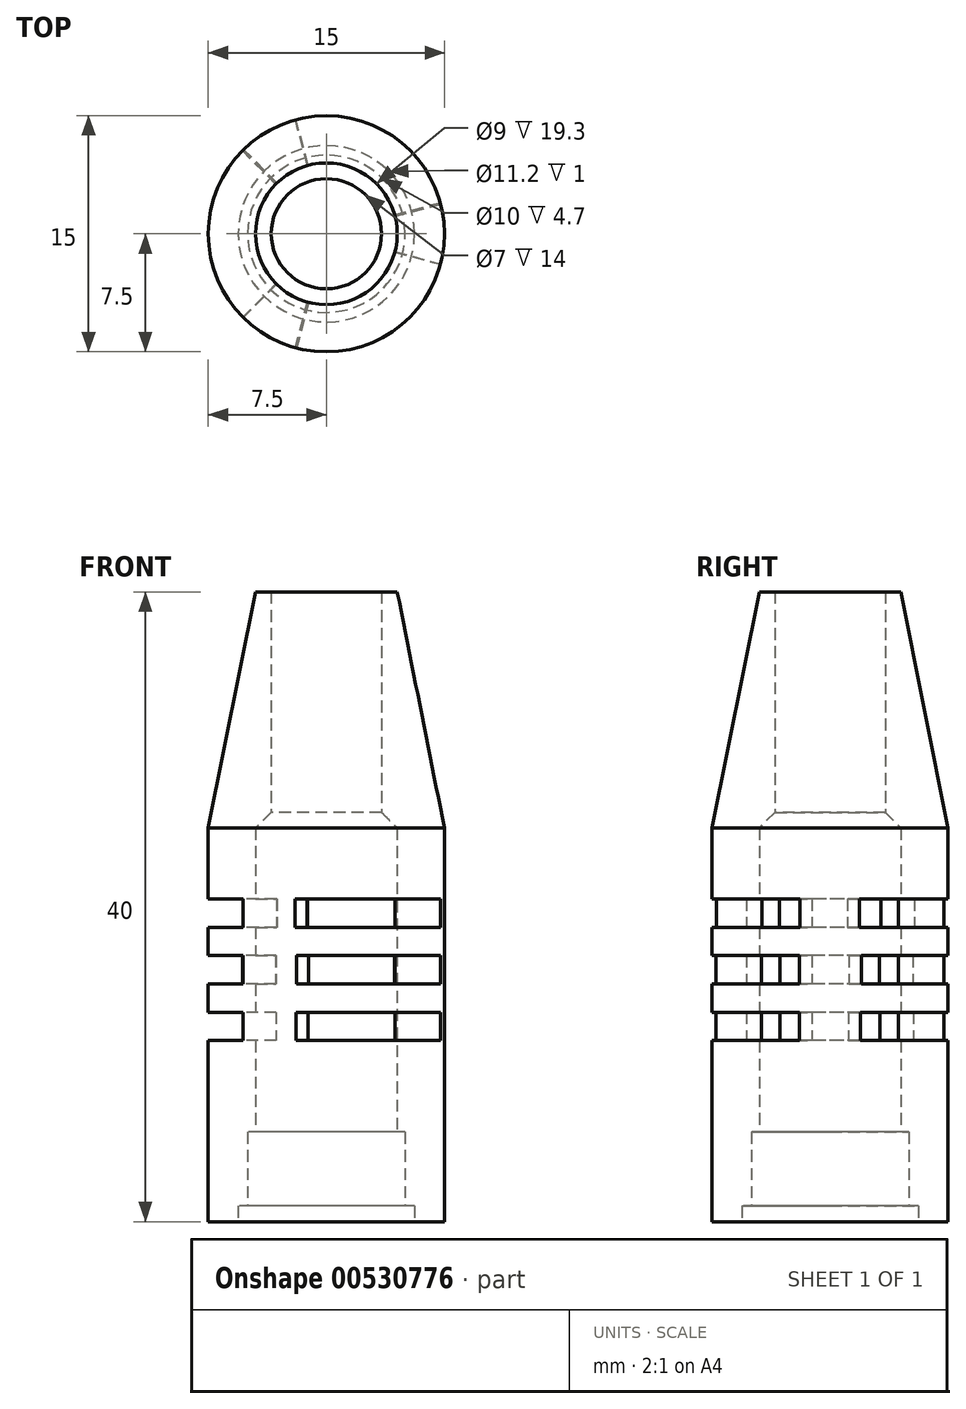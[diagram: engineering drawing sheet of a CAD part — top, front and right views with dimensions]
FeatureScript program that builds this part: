
annotation { "Feature Type Name" : "Feature", "Feature Type Description" : "" }
export const myFeature = defineFeature(function(context is Context, id is Id, definition is map)
    precondition{}
    {
        {
            var Q0;
            Q0=qCreatedBy(makeId("Top.planeOp"),FACE);
            var sketch = newSketch(context, id + "F0", { "sketchPlane" : qUnion([Q0])});
            skCircle(sketch, "E0", {"center": v(0, 0) * mm, "radius": 7.5 * mm});
            skCircle(sketch, "E1", {"center": v(0, 0) * mm, "radius": 5 * mm});
            skCircle(sketch, "E2", {"center": v(0, 0) * mm, "radius": 5.6 * mm});
            skCircle(sketch, "E3", {"center": v(0, 0) * mm, "radius": 4.5 * mm});
            skSolve(sketch);
        }
        {
            var Q0;
            Q0=makeQuery(id+"F0.imprint","IMPRINT",FACE,{"disambiguationData":[TD([[makeQuery(id+"F0.imprint","IMPRINT",EDGE,{"derivedFrom":sQuery(id+"F0.wireOp",EDGE,"E0")}),1.0]])]});
            var Q1;
            Q1=makeQuery(id+"F0.imprint","IMPRINT",FACE,{"disambiguationData":[TD([[makeQuery(id+"F0.imprint","IMPRINT",EDGE,{"derivedFrom":sQuery(id+"F0.wireOp",EDGE,"E1")}),1.0]])]});
            var Q2;
            Q2=makeQuery(id+"F0.imprint","IMPRINT",FACE,{"disambiguationData":[TD([[makeQuery(id+"F0.imprint","IMPRINT",EDGE,{"derivedFrom":sQuery(id+"F0.wireOp",EDGE,"E1")}),-1.0]])]});
            extrude(context, id + "F1", {"entities" : qUnion([Q0, Q1, Q2]), "depth" : 11.5 * mm, "offsetDistance" : 25 * mm});
        }
        {
            var Q0;
            Q0=makeQuery(id+"F0.imprint","IMPRINT",FACE,{"disambiguationData":[TD([[makeQuery(id+"F0.imprint","IMPRINT",EDGE,{"derivedFrom":sQuery(id+"F0.wireOp",EDGE,"E1")}),-1.0]])]});
            extrude(context, id + "F2", {"entities" : qUnion([Q0]), "operationType" : NewBodyOperationType.REMOVE, "oppositeDirection" : true, "depth" : -1 * mm, "offsetDistance" : 25 * mm});
        }
        {
            var Q0;
            {var subQ0=sQuery(id+"F0.wireOp",EDGE,"E3");Q0=makeQuery(id+"F2.boolean.opBoolean","SPLIT",FACE,{"disambiguationData":[TD([makeQuery(id+"F1.opExtrude","SWEPT_FACE",FACE,{"disambiguationData":[OSD([subQ0])]})])],"derivedFrom":makeQuery(id+"F1.opExtrude","CAP_FACE",FACE,{"disambiguationData":[OSD([sQuery(id+"F0.wireOp",EDGE,"E0"),subQ0])],"isStart":true})});}
            extrude(context, id + "F3", {"entities" : qUnion([Q0]), "operationType" : NewBodyOperationType.REMOVE, "oppositeDirection" : true, "depth" : 5.7 * mm, "offsetDistance" : 25 * mm});
        }
        {
            var Q0;
            Q0=makeQuery(id+"F1.opExtrude","CAP_FACE",FACE,{"disambiguationData":[OSD([sQuery(id+"F0.wireOp",EDGE,"E0"),sQuery(id+"F0.wireOp",EDGE,"E1")])],"isStart":false});
            var sketch = newSketch(context, id + "F4", { "sketchPlane" : qUnion([Q0])});
            skLineSegment(sketch, "E4", {"start": v(4.35, -1.16) * mm, "end": v(7.24, -1.94) * mm});
            skLineSegment(sketch, "E5", {"start": v(4.35, 1.16) * mm, "end": v(7.24, 1.94) * mm});
            skLineSegment(sketch, "E6.1.0", {"start": v(-1.16, 4.35) * mm, "end": v(-1.94, 7.24) * mm});
            skLineSegment(sketch, "E6.1.1", {"start": v(-3.18, 3.18) * mm, "end": v(-5.3, 5.3) * mm});
            skLineSegment(sketch, "E6.2.0", {"start": v(-3.18, -3.18) * mm, "end": v(-5.3, -5.3) * mm});
            skLineSegment(sketch, "E6.2.1", {"start": v(-1.16, -4.35) * mm, "end": v(-1.94, -7.24) * mm});
            skPoint(sketch, "E6.center", {"position": v(0, 0) * mm});
            skSolve(sketch);
        }
        {
            var Q0;
            {var subQ0=sQuery(id+"F4.wireOp",EDGE,"E6.1.0");Q0=makeQuery(id+"F4.imprint","IMPRINT",FACE,{"disambiguationData":[TD([[makeQuery(id+"F4.imprint","IMPRINT",EDGE,{"derivedFrom":subQ0}),1.0]])]});}
            var Q1;
            {var subQ0=sQuery(id+"F4.wireOp",EDGE,"E6.2.0");Q1=makeQuery(id+"F4.imprint","IMPRINT",FACE,{"disambiguationData":[TD([[makeQuery(id+"F4.imprint","IMPRINT",EDGE,{"derivedFrom":subQ0}),1.0]])]});}
            var Q2;
            {var subQ0=sQuery(id+"F4.wireOp",EDGE,"E4");Q2=makeQuery(id+"F4.imprint","IMPRINT",FACE,{"disambiguationData":[TD([[makeQuery(id+"F4.imprint","IMPRINT",EDGE,{"derivedFrom":subQ0}),1.0]])]});}
            extrude(context, id + "F5", {"entities" : qUnion([Q0, Q1, Q2]), "operationType" : NewBodyOperationType.ADD, "depth" : 1.8 * mm, "offsetDistance" : 25 * mm});
        }
        {
            var Q0;
            Q0=makeQuery(id+"F5.opExtrude","CAP_FACE",FACE,{"disambiguationData":[OSD([sQuery(id+"F0.wireOp",EDGE,"E0"),sQuery(id+"F0.wireOp",EDGE,"E1"),sQuery(id+"F4.wireOp",EDGE,"E4"),sQuery(id+"F4.wireOp",EDGE,"E5")])],"isStart":false});
            var sketch = newSketch(context, id + "F6", { "sketchPlane" : qUnion([Q0])});
            skCircle(sketch, "E7", {"center": v(0, 0) * mm, "radius": 7.5 * mm});
            skCircle(sketch, "E8", {"center": v(0, 0) * mm, "radius": 4.5 * mm});
            skSolve(sketch);
        }
        {
            var Q0;
            Q0 = qSketchRegion(id + "F6", true);
            extrude(context, id + "F7", {"entities" : qUnion([Q0]), "operationType" : NewBodyOperationType.ADD, "depth" : 1.8 * mm, "offsetDistance" : 25 * mm});
        }
        {
            var Q0;
            Q0=makeQuery(id+"F7.opExtrude","CAP_FACE",FACE,{"disambiguationData":[OSD([sQuery(id+"F6.wireOp",EDGE,"E7"),sQuery(id+"F6.wireOp",EDGE,"E8")])],"isStart":false});
            var sketch = newSketch(context, id + "F8", { "sketchPlane" : qUnion([Q0])});
            skPoint(sketch, "E9.center", {"position": v(1.29, 0.16) * mm});
            skLineSegment(sketch, "E10", {"start": v(4.35, -1.17) * mm, "end": v(7.24, -1.94) * mm});
            skLineSegment(sketch, "E11", {"start": v(4.33, 1.2) * mm, "end": v(7.23, 1.99) * mm});
            skLineSegment(sketch, "E12.1.0", {"start": v(-3.21, 3.15) * mm, "end": v(-5.34, 5.27) * mm});
            skLineSegment(sketch, "E12.1.1", {"start": v(-1.16, 4.35) * mm, "end": v(-1.94, 7.24) * mm});
            skLineSegment(sketch, "E12.2.0", {"start": v(-1.12, -4.36) * mm, "end": v(-1.9, -7.26) * mm});
            skLineSegment(sketch, "E12.2.1", {"start": v(-3.18, -3.18) * mm, "end": v(-5.3, -5.3) * mm});
            skPoint(sketch, "E12.center", {"position": v(0, 0) * mm});
            skSolve(sketch);
        }
        {
            var Q0;
            {var subQ0=sQuery(id+"F8.wireOp",EDGE,"E10");Q0=makeQuery(id+"F8.imprint","IMPRINT",FACE,{"disambiguationData":[TD([[makeQuery(id+"F8.imprint","IMPRINT",EDGE,{"derivedFrom":subQ0}),1.0]])]});}
            var Q1;
            {var subQ0=sQuery(id+"F8.wireOp",EDGE,"E12.1.0");Q1=makeQuery(id+"F8.imprint","IMPRINT",FACE,{"disambiguationData":[TD([[makeQuery(id+"F8.imprint","IMPRINT",EDGE,{"derivedFrom":subQ0}),-1.0]])]});}
            var Q2;
            {var subQ0=sQuery(id+"F8.wireOp",EDGE,"E12.2.0");Q2=makeQuery(id+"F8.imprint","IMPRINT",FACE,{"disambiguationData":[TD([[makeQuery(id+"F8.imprint","IMPRINT",EDGE,{"derivedFrom":subQ0}),-1.0]])]});}
            extrude(context, id + "F9", {"entities" : qUnion([Q0, Q1, Q2]), "operationType" : NewBodyOperationType.ADD, "depth" : 1.8 * mm, "offsetDistance" : 25 * mm});
        }
        {
            var Q0;
            Q0=makeQuery(id+"F9.opExtrude","CAP_FACE",FACE,{"disambiguationData":[OSD([sQuery(id+"F6.wireOp",EDGE,"E7"),sQuery(id+"F6.wireOp",EDGE,"E8"),sQuery(id+"F8.wireOp",EDGE,"VKkFFFKs-lQaI-sclN-VApt-fjEv4aChX7Hu"),sQuery(id+"F8.wireOp",EDGE,"ZannldDg-Nn5e-IlUL-YRys-QU4dFc9HWdYi")])],"isStart":false});
            var sketch = newSketch(context, id + "F10", { "sketchPlane" : qUnion([Q0])});
            skCircle(sketch, "E13", {"center": v(0, 0) * mm, "radius": 7.5 * mm});
            skCircle(sketch, "E14", {"center": v(0, 0) * mm, "radius": 4.5 * mm});
            skSolve(sketch);
        }
        {
            var Q0;
            Q0 = qSketchRegion(id + "F10", true);
            extrude(context, id + "F11", {"entities" : qUnion([Q0]), "operationType" : NewBodyOperationType.ADD, "depth" : 1.8 * mm, "offsetDistance" : 25 * mm});
        }
        {
            var Q0;
            Q0=makeQuery(id+"F11.opExtrude","CAP_FACE",FACE,{"disambiguationData":[OSD([sQuery(id+"F10.wireOp",EDGE,"E13"),sQuery(id+"F10.wireOp",EDGE,"E14")])],"isStart":false});
            var sketch = newSketch(context, id + "F12", { "sketchPlane" : qUnion([Q0])});
            skPoint(sketch, "E15.center", {"position": v(0.1, 0) * mm});
            skLineSegment(sketch, "E16", {"start": v(4.36, 1.1) * mm, "end": v(7.26, 1.88) * mm});
            skLineSegment(sketch, "E17", {"start": v(4.35, -1.14) * mm, "end": v(7.25, -1.91) * mm});
            skLineSegment(sketch, "E18.1.0", {"start": v(-3.14, 3.23) * mm, "end": v(-5.26, 5.35) * mm});
            skLineSegment(sketch, "E18.1.1", {"start": v(-1.2, 4.34) * mm, "end": v(-1.97, 7.24) * mm});
            skLineSegment(sketch, "E18.2.0", {"start": v(-1.22, -4.33) * mm, "end": v(-2, -7.23) * mm});
            skLineSegment(sketch, "E18.2.1", {"start": v(-3.16, -3.2) * mm, "end": v(-5.28, -5.32) * mm});
            skPoint(sketch, "E18.center", {"position": v(0, 0) * mm});
            skSolve(sketch);
        }
        {
            var Q0;
            {var subQ0=sQuery(id+"F12.wireOp",EDGE,"E18.1.0");Q0=makeQuery(id+"F12.imprint","IMPRINT",FACE,{"disambiguationData":[TD([[makeQuery(id+"F12.imprint","IMPRINT",EDGE,{"derivedFrom":subQ0}),-1.0]])]});}
            var Q1;
            {var subQ0=sQuery(id+"F12.wireOp",EDGE,"E16");Q1=makeQuery(id+"F12.imprint","IMPRINT",FACE,{"disambiguationData":[TD([[makeQuery(id+"F12.imprint","IMPRINT",EDGE,{"derivedFrom":subQ0}),-1.0]])]});}
            var Q2;
            {var subQ0=sQuery(id+"F12.wireOp",EDGE,"E18.2.0");Q2=makeQuery(id+"F12.imprint","IMPRINT",FACE,{"disambiguationData":[TD([[makeQuery(id+"F12.imprint","IMPRINT",EDGE,{"derivedFrom":subQ0}),-1.0]])]});}
            extrude(context, id + "F13", {"entities" : qUnion([Q0, Q1, Q2]), "operationType" : NewBodyOperationType.ADD, "depth" : 1.8 * mm, "offsetDistance" : 25 * mm});
        }
        {
            var Q0;
            Q0=makeQuery(id+"F13.opExtrude","CAP_FACE",FACE,{"disambiguationData":[OSD([sQuery(id+"F10.wireOp",EDGE,"E13"),sQuery(id+"F10.wireOp",EDGE,"E14"),sQuery(id+"F12.wireOp",EDGE,"E15.2.0"),sQuery(id+"F12.wireOp",EDGE,"E15.2.1")])],"isStart":false});
            var sketch = newSketch(context, id + "F14", { "sketchPlane" : qUnion([Q0])});
            skCircle(sketch, "E19", {"center": v(0, 0) * mm, "radius": 7.5 * mm});
            skCircle(sketch, "E20", {"center": v(0, 0) * mm, "radius": 4.5 * mm});
            skSolve(sketch);
        }
        {
            var Q0;
            Q0 = qSketchRegion(id + "F14", true);
            extrude(context, id + "F15", {"entities" : qUnion([Q0]), "operationType" : NewBodyOperationType.ADD, "depth" : 4.5 * mm, "offsetDistance" : 25 * mm});
        }
        {
            var Q0;
            Q0=makeQuery(id+"F15.opExtrude","CAP_FACE",FACE,{"disambiguationData":[OSD([sQuery(id+"F14.wireOp",EDGE,"E19"),sQuery(id+"F14.wireOp",EDGE,"E20")])],"isStart":false});
            var sketch = newSketch(context, id + "F16", { "sketchPlane" : qUnion([Q0])});
            skCircle(sketch, "E21", {"center": v(0, 0) * mm, "radius": 7.5 * mm});
            skCircle(sketch, "E22", {"center": v(0, 0) * mm, "radius": 3.5 * mm});
            skSolve(sketch);
        }
        {
            var Q0;
            Q0 = qSketchRegion(id + "F16", true);
            extrude(context, id + "F17", {"entities" : qUnion([Q0]), "operationType" : NewBodyOperationType.ADD, "depth" : 15 * mm, "offsetDistance" : 25 * mm});
        }
        {
            var Q0;
            Q0=makeQuery(id+"F17.opExtrude","CAP_EDGE",EDGE,{"disambiguationData":[OSD([sQuery(id+"F16.wireOp",EDGE,"E21")])],"isStart":false});
            chamfer(context, id + "F18", {"entities" : qUnion([Q0]), "chamferType" : ChamferType.TWO_OFFSETS, "width1" : 3 * mm, "oppositeDirection" : false, "width2" : 15 * mm, "tangentPropagation" : true});
        }
        {
            var Q0;
            Q0=makeQuery(id+"F17.opExtrude","CAP_EDGE",EDGE,{"disambiguationData":[OSD([sQuery(id+"F16.wireOp",EDGE,"E22")])],"isStart":true});
            chamfer(context, id + "F19", {"entities" : qUnion([Q0]), "width" : 1 * mm, "tangentPropagation" : true});
        }
    });
